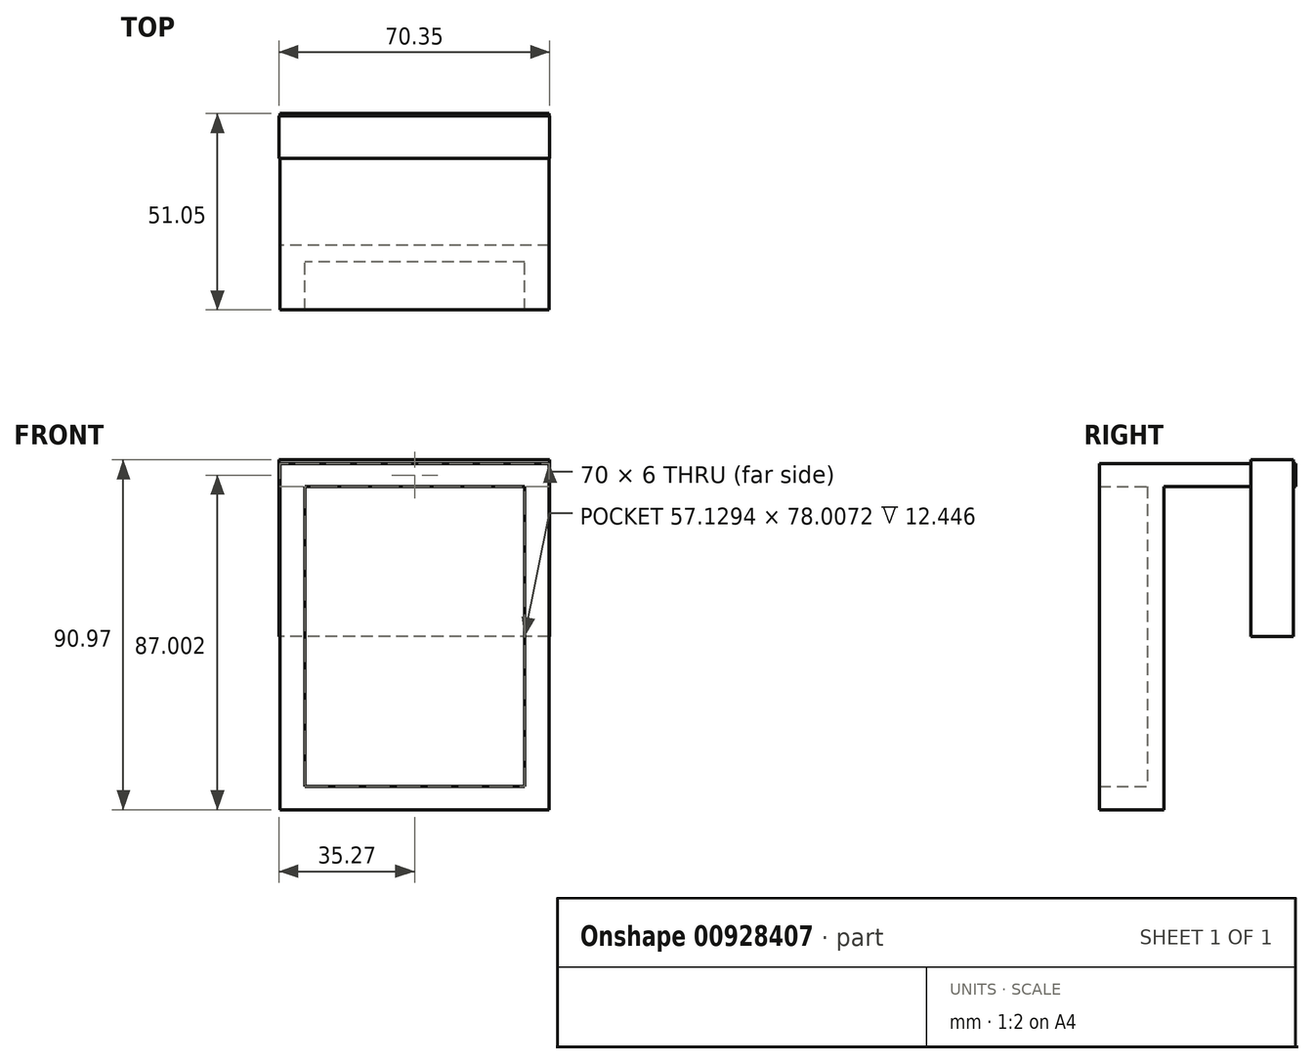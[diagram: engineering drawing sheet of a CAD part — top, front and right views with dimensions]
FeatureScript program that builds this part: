
annotation { "Feature Type Name" : "Feature", "Feature Type Description" : "" }
export const myFeature = defineFeature(function(context is Context, id is Id, definition is map)
    precondition{}
    {
        {
            var Q0;
            Q0=qCreatedBy(makeId("Front.planeOp"),FACE);
            var sketch = newSketch(context, id + "F0", { "sketchPlane" : qUnion([Q0])});
            skLineSegment(sketch, "E0.bottom", {"start": v(35, 45) * mm, "end": v(-35, 45) * mm});
            skLineSegment(sketch, "E0.top", {"start": v(35, -45) * mm, "end": v(-35, -45) * mm});
            skLineSegment(sketch, "E0.left", {"start": v(35, 45) * mm, "end": v(35, -45) * mm});
            skLineSegment(sketch, "E0.right", {"start": v(-35, 45) * mm, "end": v(-35, -45) * mm});
            skPoint(sketch, "E0.middle", {"position": v(0, 0) * mm});
            skLineSegment(sketch, "E1.bottom", {"start": v(28.56, 39) * mm, "end": v(-28.56, 39) * mm});
            skLineSegment(sketch, "E1.top", {"start": v(28.56, -39) * mm, "end": v(-28.56, -39) * mm});
            skLineSegment(sketch, "E1.left", {"start": v(28.56, 39) * mm, "end": v(28.56, -39) * mm});
            skLineSegment(sketch, "E1.right", {"start": v(-28.56, 39) * mm, "end": v(-28.56, -39) * mm});
            skLineSegment(sketch, "E2.bottom", {"start": v(-35, 45) * mm, "end": v(35, 45) * mm});
            skLineSegment(sketch, "E2.top", {"start": v(-35, 39) * mm, "end": v(35, 39) * mm});
            skLineSegment(sketch, "E2.left", {"start": v(-35, 45) * mm, "end": v(-35, 39) * mm});
            skLineSegment(sketch, "E2.right", {"start": v(35, 45) * mm, "end": v(35, 39) * mm});
            skSolve(sketch);
        }
        {
            var Q0;
            {var subQ1=sQuery(id+"F0.wireOp",EDGE,"E0.top");var subQ11=sQuery(id+"F0.wireOp",EDGE,"E0.bottom");Q0=qUnion([makeQuery(id+"F0.imprint","IMPRINT",FACE,{"disambiguationData":[TD([[makeQuery(id+"F0.imprint","IMPRINT",EDGE,{"derivedFrom":subQ11}),1.0]])]}),makeQuery(id+"F0.imprint","IMPRINT",FACE,{"disambiguationData":[TD([[makeQuery(id+"F0.imprint","IMPRINT",EDGE,{"derivedFrom":subQ1}),-1.0]])]})]);}
            extrude(context, id + "F1", {"entities" : qUnion([Q0]), "depth" : 16.76 * mm, "offsetDistance" : 25.4 * mm});
        }
        {
            var Q0;
            Q0=qCreatedBy(makeId("Front.planeOp"),FACE);
            var sketch = newSketch(context, id + "F2", { "sketchPlane" : qUnion([Q0])});
            skLineSegment(sketch, "E3.bottom", {"start": v(35, 45) * mm, "end": v(-35, 45) * mm});
            skLineSegment(sketch, "E3.top", {"start": v(35, -45) * mm, "end": v(-35, -45) * mm});
            skLineSegment(sketch, "E3.left", {"start": v(35, 45) * mm, "end": v(35, -45) * mm});
            skLineSegment(sketch, "E3.right", {"start": v(-35, 45) * mm, "end": v(-35, -45) * mm});
            skPoint(sketch, "E3.middle", {"position": v(0, 0) * mm});
            skSolve(sketch);
        }
        {
            var Q0;
            Q0=qSketchRegion(id+"F2",true);
            extrude(context, id + "F3", {"entities" : qUnion([Q0]), "operationType" : NewBodyOperationType.ADD, "depth" : 4.32 * mm, "offsetDistance" : 25.4 * mm});
        }
        {
            var Q0;
            {var subQ2=sQuery(id+"F0.wireOp",EDGE,"E0.bottom");Q0=makeQuery(id+"F0.imprint","IMPRINT",FACE,{"disambiguationData":[TD([[makeQuery(id+"F0.imprint","IMPRINT",EDGE,{"derivedFrom":subQ2}),1.0]])]});}
            extrude(context, id + "F4", {"entities" : qUnion([Q0]), "operationType" : NewBodyOperationType.ADD, "oppositeDirection" : true, "depth" : 34.3 * mm, "offsetDistance" : 25.4 * mm});
        }
        {
            var Q0;
            Q0=qCreatedBy(makeId("Top.planeOp"),FACE);
            var sketch = newSketch(context, id + "F5", { "sketchPlane" : qUnion([Q0])});
            skLineSegment(sketch, "E4.bottom", {"start": v(35.08, 33.74) * mm, "end": v(-35.27, 33.74) * mm});
            skLineSegment(sketch, "E4.top", {"start": v(35.08, 22.65) * mm, "end": v(-35.27, 22.65) * mm});
            skLineSegment(sketch, "E4.left", {"start": v(35.08, 33.74) * mm, "end": v(35.08, 22.65) * mm});
            skLineSegment(sketch, "E4.right", {"start": v(-35.27, 33.74) * mm, "end": v(-35.27, 22.65) * mm});
            skSolve(sketch);
        }
        {
            var Q0;
            Q0 = qSketchRegion(id + "F5", true);
            extrude(context, id + "F6", {"entities" : qUnion([Q0]), "operationType" : NewBodyOperationType.ADD, "depth" : 45.97 * mm, "offsetDistance" : 25.4 * mm});
        }
    });
